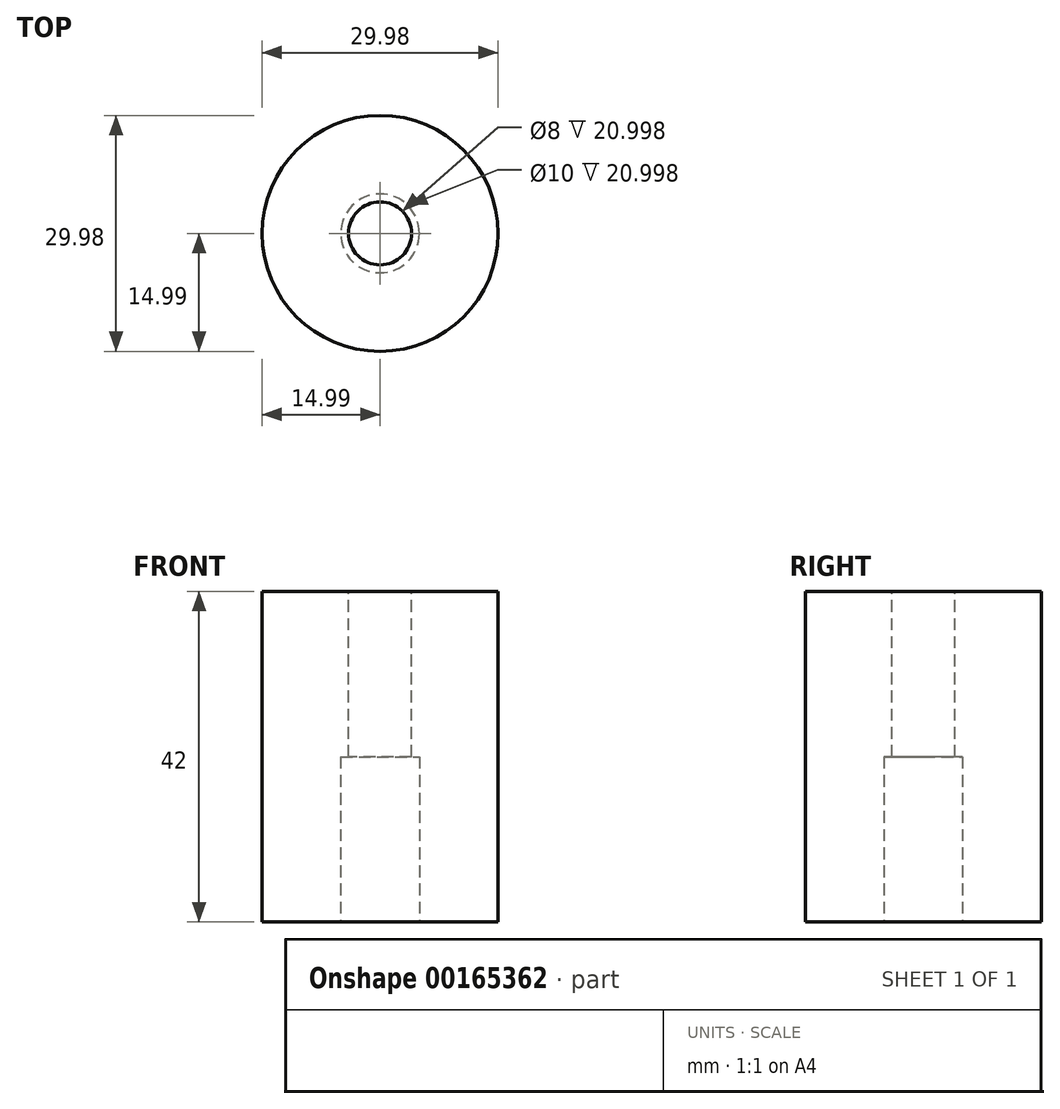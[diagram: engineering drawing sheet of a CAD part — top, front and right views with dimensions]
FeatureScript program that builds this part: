
annotation { "Feature Type Name" : "Feature", "Feature Type Description" : "" }
export const myFeature = defineFeature(function(context is Context, id is Id, definition is map)
    precondition{}
    {
        {
            var Q0;
            Q0=qCreatedBy(makeId("Top.planeOp"),FACE);
            var sketch = newSketch(context, id + "F0", { "sketchPlane" : qUnion([Q0])});
            skCircle(sketch, "E0", {"center": v(0, 0) * mm, "radius": 14.99 * mm});
            skSolve(sketch);
        }
        {
            var Q0;
            Q0=qSketchRegion(id+"F0",true);
            extrude(context, id + "F1", {"entities" : qUnion([Q0]), "depth" : 42 * mm});
        }
        {
            var Q0;
            Q0=qCreatedBy(makeId("Top.planeOp"),FACE);
            var sketch = newSketch(context, id + "F2", { "sketchPlane" : qUnion([Q0])});
            skCircle(sketch, "E1", {"center": v(0, 0) * mm, "radius": 4 * mm});
            skSolve(sketch);
        }
        {
            var Q0;
            Q0=qSketchRegion(id+"F2",true);
            extrude(context, id + "F3", {"entities" : qUnion([Q0]), "operationType" : NewBodyOperationType.REMOVE, "oppositeDirection" : true, "depth" : 15 * mm});
        }
        {
            var Q0;
            Q0=makeQuery(id+"F1.opExtrude","CAP_FACE",FACE,{"disambiguationData":[OSD([sQuery(id+"F0.wireOp",EDGE,"E0")])],"isStart":false});
            var sketch = newSketch(context, id + "F4", { "sketchPlane" : qUnion([Q0])});
            skCircle(sketch, "E2", {"center": v(0, 0) * mm, "radius": 4 * mm});
            skSolve(sketch);
        }
        {
            var Q0;
            Q0=qSketchRegion(id+"F4",true);
            extrude(context, id + "F5", {"entities" : qUnion([Q0]), "operationType" : NewBodyOperationType.REMOVE, "oppositeDirection" : true, "depth" : 21 * mm});
        }
        {
            var Q0;
            Q0=makeQuery(id+"F1.opExtrude","CAP_FACE",FACE,{"disambiguationData":[OSD([sQuery(id+"F0.wireOp",EDGE,"E0")])],"isStart":true});
            var sketch = newSketch(context, id + "F6", { "sketchPlane" : qUnion([Q0])});
            skCircle(sketch, "E3", {"center": v(0, 0) * mm, "radius": 5 * mm});
            skSolve(sketch);
        }
        {
            var Q0;
            Q0=qSketchRegion(id+"F6",true);
            extrude(context, id + "F7", {"entities" : qUnion([Q0]), "operationType" : NewBodyOperationType.REMOVE, "oppositeDirection" : true, "depth" : 21 * mm});
        }
    });
